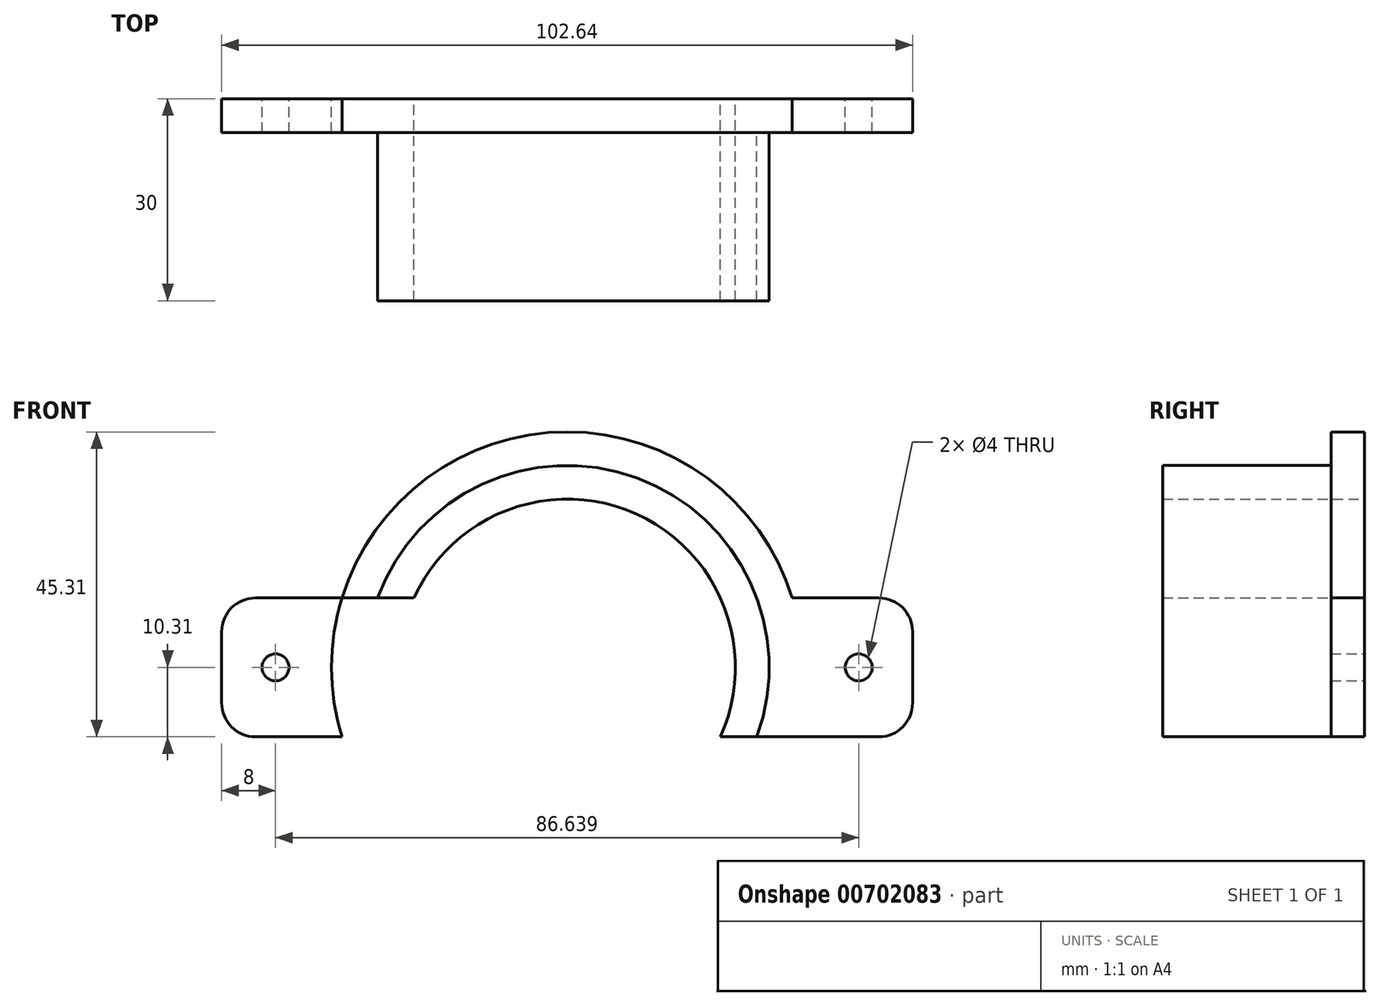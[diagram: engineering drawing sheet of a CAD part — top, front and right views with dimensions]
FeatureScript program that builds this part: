
annotation { "Feature Type Name" : "Feature", "Feature Type Description" : "" }
export const myFeature = defineFeature(function(context is Context, id is Id, definition is map)
    precondition{}
    {
        {
            var Q0;
            Q0=qCreatedBy(makeId("Front.planeOp"),FACE);
            var sketch = newSketch(context, id + "F0", { "sketchPlane" : qUnion([Q0])});
            skCircle(sketch, "E0", {"center": v(0, 0) * mm, "radius": 25 * mm});
            skCircle(sketch, "E1.0", {"center": v(0, 0) * mm, "radius": 30 * mm});
            skCircle(sketch, "E2.0", {"center": v(0, 0) * mm, "radius": 35 * mm});
            skLineSegment(sketch, "E3.bottom", {"start": v(46.32, 10.31) * mm, "end": v(-46.32, 10.31) * mm});
            skLineSegment(sketch, "E3.top", {"start": v(46.32, -10.31) * mm, "end": v(-46.32, -10.31) * mm});
            skLineSegment(sketch, "E3.left", {"start": v(51.32, 5.31) * mm, "end": v(51.32, -5.31) * mm});
            skLineSegment(sketch, "E3.right", {"start": v(-51.32, 5.31) * mm, "end": v(-51.32, -5.31) * mm});
            skPoint(sketch, "E4.visualSharp", {"position": v(-51.32, 10.31) * mm});
            skArc(sketch, "E4.filletArc", {"start": v(-46.32, 10.31) * mm, "mid": v(-49.86, 8.85) * mm, "end": v(-51.32, 5.31) * mm});
            skPoint(sketch, "E5.visualSharp", {"position": v(-51.32, -10.31) * mm});
            skArc(sketch, "E5.filletArc", {"start": v(-51.32, -5.31) * mm, "mid": v(-49.86, -8.85) * mm, "end": v(-46.32, -10.31) * mm});
            skPoint(sketch, "E6.visualSharp", {"position": v(51.32, -10.31) * mm});
            skArc(sketch, "E6.filletArc", {"start": v(46.32, -10.31) * mm, "mid": v(49.86, -8.85) * mm, "end": v(51.32, -5.31) * mm});
            skPoint(sketch, "E7.visualSharp", {"position": v(51.32, 10.31) * mm});
            skArc(sketch, "E7.filletArc", {"start": v(51.32, 5.31) * mm, "mid": v(49.86, 8.85) * mm, "end": v(46.32, 10.31) * mm});
            skCircle(sketch, "E8", {"center": v(-43.32, 0) * mm, "radius": 2 * mm});
            skCircle(sketch, "E9", {"center": v(43.32, 0) * mm, "radius": 2 * mm});
            skSolve(sketch);
        }
        {
            var Q0;
            {var subQ0=sQuery(id+"F0.wireOp",EDGE,"E3.bottom");var subQ1=sQuery(id+"F0.wireOp",EDGE,"E0");var subQ2=makeQuery(id+"F0.imprint","INTERSECT",VERTEX,{"disambiguationData":[OD(0.0)],"derivedFrom":[subQ1,subQ0]});Q0=makeQuery(id+"F0.imprint","IMPRINT",FACE,{"disambiguationData":[TD([[makeQuery(id+"F0.imprint","IMPRINT",EDGE,{"disambiguationData":[TD([[subQ2,1.0]])],"derivedFrom":subQ1}),-1.0]])]});}
            var Q1;
            {var subQ0=sQuery(id+"F0.wireOp",EDGE,"E3.top");var subQ1=sQuery(id+"F0.wireOp",EDGE,"E0");var subQ2=makeQuery(id+"F0.imprint","INTERSECT",VERTEX,{"disambiguationData":[OD(0.0)],"derivedFrom":[subQ1,subQ0]});Q1=makeQuery(id+"F0.imprint","IMPRINT",FACE,{"disambiguationData":[TD([[makeQuery(id+"F0.imprint","IMPRINT",EDGE,{"disambiguationData":[TD([[subQ2,-1.0]])],"derivedFrom":subQ1}),-1.0]])]});}
            var Q2;
            {var subQ0=sQuery(id+"F0.wireOp",EDGE,"E3.bottom");var subQ1=sQuery(id+"F0.wireOp",EDGE,"E0");var subQ2=makeQuery(id+"F0.imprint","INTERSECT",VERTEX,{"disambiguationData":[OD(0.0)],"derivedFrom":[subQ1,subQ0]});Q2=makeQuery(id+"F0.imprint","IMPRINT",FACE,{"disambiguationData":[TD([[makeQuery(id+"F0.imprint","IMPRINT",EDGE,{"disambiguationData":[TD([[subQ2,-1.0]])],"derivedFrom":subQ1}),-1.0]])]});}
            var Q3;
            {var subQ0=sQuery(id+"F0.wireOp",EDGE,"E3.bottom");var subQ1=sQuery(id+"F0.wireOp",EDGE,"E0");var subQ2=makeQuery(id+"F0.imprint","INTERSECT",VERTEX,{"disambiguationData":[OD(1.0)],"derivedFrom":[subQ1,subQ0]});Q3=makeQuery(id+"F0.imprint","IMPRINT",FACE,{"disambiguationData":[TD([[makeQuery(id+"F0.imprint","IMPRINT",EDGE,{"disambiguationData":[TD([[subQ2,1.0]])],"derivedFrom":subQ1}),-1.0]])]});}
            extrude(context, id + "F1", {"entities" : qUnion([Q0, Q1, Q2, Q3]), "depth" : 30 * mm, "offsetDistance" : 25 * mm});
        }
        {
            var Q0;
            {var subQ0=sQuery(id+"F0.wireOp",EDGE,"E3.bottom");var subQ1=sQuery(id+"F0.wireOp",EDGE,"E1.0");var subQ2=makeQuery(id+"F0.imprint","INTERSECT",VERTEX,{"disambiguationData":[OD(0.0)],"derivedFrom":[subQ1,subQ0]});Q0=makeQuery(id+"F0.imprint","IMPRINT",FACE,{"disambiguationData":[TD([[makeQuery(id+"F0.imprint","IMPRINT",EDGE,{"disambiguationData":[TD([[subQ2,-1.0]])],"derivedFrom":subQ1}),-1.0]])]});}
            var Q1;
            {var subQ0=sQuery(id+"F0.wireOp",EDGE,"E3.bottom");var subQ1=sQuery(id+"F0.wireOp",EDGE,"E1.0");var subQ2=makeQuery(id+"F0.imprint","INTERSECT",VERTEX,{"disambiguationData":[OD(0.0)],"derivedFrom":[subQ1,subQ0]});Q1=makeQuery(id+"F0.imprint","IMPRINT",FACE,{"disambiguationData":[TD([[makeQuery(id+"F0.imprint","IMPRINT",EDGE,{"disambiguationData":[TD([[subQ2,1.0]])],"derivedFrom":subQ1}),-1.0]])]});}
            var Q2;
            {var subQ0=sQuery(id+"F0.wireOp",EDGE,"E3.bottom");var subQ1=sQuery(id+"F0.wireOp",EDGE,"E1.0");var subQ2=makeQuery(id+"F0.imprint","INTERSECT",VERTEX,{"disambiguationData":[OD(1.0)],"derivedFrom":[subQ1,subQ0]});Q2=makeQuery(id+"F0.imprint","IMPRINT",FACE,{"disambiguationData":[TD([[makeQuery(id+"F0.imprint","IMPRINT",EDGE,{"disambiguationData":[TD([[subQ2,1.0]])],"derivedFrom":subQ1}),-1.0]])]});}
            var Q3;
            {var subQ0=sQuery(id+"F0.wireOp",EDGE,"E3.top");var subQ1=sQuery(id+"F0.wireOp",EDGE,"E1.0");var subQ2=makeQuery(id+"F0.imprint","INTERSECT",VERTEX,{"disambiguationData":[OD(0.0)],"derivedFrom":[subQ1,subQ0]});Q3=makeQuery(id+"F0.imprint","IMPRINT",FACE,{"disambiguationData":[TD([[makeQuery(id+"F0.imprint","IMPRINT",EDGE,{"disambiguationData":[TD([[subQ2,-1.0]])],"derivedFrom":subQ1}),-1.0]])]});}
            var Q4;
            Q4=makeQuery(id+"F0.imprint","IMPRINT",FACE,{"disambiguationData":[TD([[makeQuery(id+"F0.imprint","IMPRINT",EDGE,{"derivedFrom":sQuery(id+"F0.wireOp",EDGE,"E3.right")}),1.0]])]});
            var Q5;
            Q5=makeQuery(id+"F0.imprint","IMPRINT",FACE,{"disambiguationData":[TD([[makeQuery(id+"F0.imprint","IMPRINT",EDGE,{"derivedFrom":sQuery(id+"F0.wireOp",EDGE,"E3.left")}),-1.0]])]});
            extrude(context, id + "F2", {"entities" : qUnion([Q0, Q1, Q2, Q3, Q4, Q5]), "operationType" : NewBodyOperationType.ADD, "depth" : 5 * mm, "offsetDistance" : 25 * mm});
        }
    });
